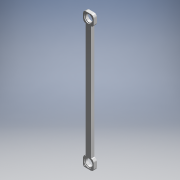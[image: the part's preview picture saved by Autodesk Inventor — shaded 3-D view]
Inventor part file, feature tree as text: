
AUTODESK INVENTOR PART (.ipt)
format: ipt  version: 2016 (Build 200138000, 138)  size: 162,304 bytes
history: native  units: mm (DEFAULTED — no unit token found)
features: extrude x3, fillet x2, sketch x2, hole x1
ambient origin geometry x8: Origin, YZ Plane, XZ Plane, XY Plane, X Axis, Y Axis, Z Axis, Center Point
bodies: Solid1 (feature_tree)
feature tree (8):
  extrude  "Extrusion1"  Depth=330.2mm
  extrude  "Extrusion2"  Depth=12.7mm
  extrude  "Extrusion5"  Depth=7.9375mm TaperAngle=0.0deg
  hole  "Hole2"  [1 undecoded]
  fillet  "Fillet1"  Radius=20.6375mm
  fillet  "Fillet2"  Radius=1.5875mm
  sketch  "Sketch2"  dims[d0=25.4mm d1=330.2mm]
  sketch  "Sketch6"  dims[d2=17.4625mm d3=12.7mm d4=7.9375mm d5=0.0mm d8=25.4mm d9=0.0mm d14=20.6375mm d17=1.5875mm d18=0.0mm d30=5.08mm d31=4.1402mm d32=10.0076mm d33=9.525mm d34=6.35mm d35=14.3117mm d36=14.1986mm d37=20.594885mm d38=6.35mm d39=3.175mm d40=17.4625mm d41=12.7mm d42=12.7mm d45=279.4mm d46=25.4mm d47=6.35mm d48=279.4mm d49=25.4mm d50=6.35mm d51=20.6375mm]
note: 1 required parameter value undecoded (feature->parameter linkage not recoverable at this tier; creation-order binding heuristic only, values carry confidence <= 0.55)
